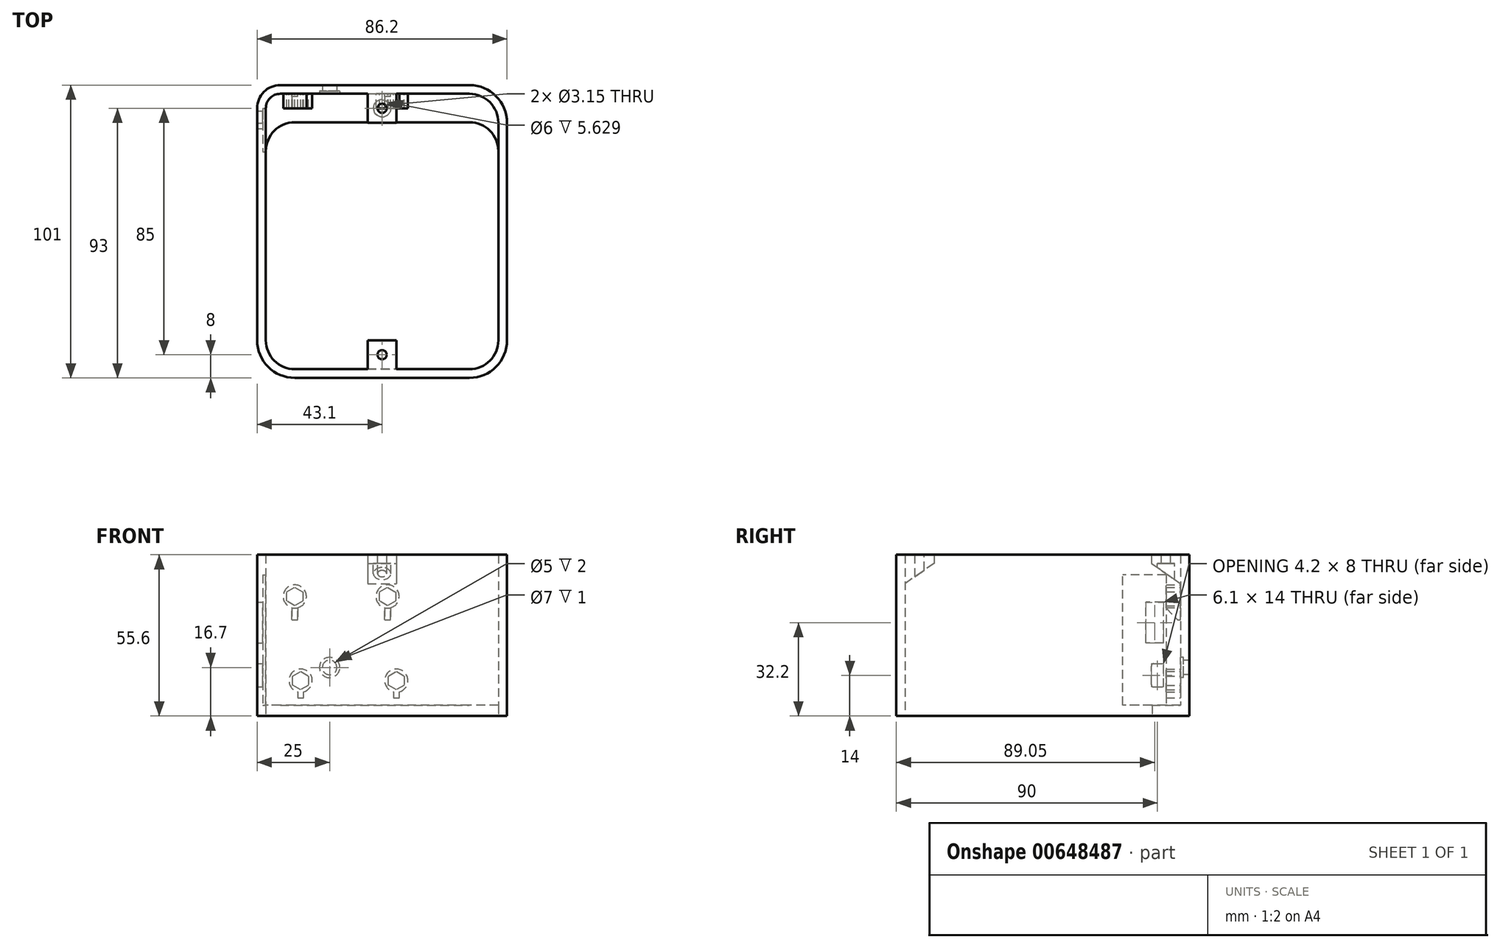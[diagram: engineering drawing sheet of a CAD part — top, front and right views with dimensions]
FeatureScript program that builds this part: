
annotation { "Feature Type Name" : "Feature", "Feature Type Description" : "" }
export const myFeature = defineFeature(function(context is Context, id is Id, definition is map)
    precondition{}
    {
        {
            var Q0;
            Q0=qCreatedBy(makeId("Top.planeOp"),FACE);
            var sketch = newSketch(context, id + "F0", { "sketchPlane" : qUnion([Q0])});
            skLineSegment(sketch, "E0.bottom", {"start": v(30.1, 37.7) * mm, "end": v(-30.1, 37.7) * mm});
            skLineSegment(sketch, "E0.top", {"start": v(30.1, -47.5) * mm, "end": v(-30.1, -47.5) * mm});
            skLineSegment(sketch, "E0.left", {"start": v(40.1, 27.7) * mm, "end": v(40.1, -37.5) * mm});
            skLineSegment(sketch, "E0.right", {"start": v(-40.1, 27.7) * mm, "end": v(-40.1, -37.5) * mm});
            skPoint(sketch, "E0.middle", {"position": v(0, 0) * mm});
            skPoint(sketch, "E1.visualSharp", {"position": v(-40.1, 37.7) * mm});
            skArc(sketch, "E1.filletArc", {"start": v(-30.1, 37.7) * mm, "mid": v(-37.17, 34.77) * mm, "end": v(-40.1, 27.7) * mm});
            skPoint(sketch, "E2.visualSharp", {"position": v(-40.1, -47.5) * mm});
            skArc(sketch, "E2.filletArc", {"start": v(-40.1, -37.5) * mm, "mid": v(-37.17, -44.57) * mm, "end": v(-30.1, -47.5) * mm});
            skPoint(sketch, "E3.visualSharp", {"position": v(40.1, -47.5) * mm});
            skArc(sketch, "E3.filletArc", {"start": v(30.1, -47.5) * mm, "mid": v(37.17, -44.57) * mm, "end": v(40.1, -37.5) * mm});
            skPoint(sketch, "E4.visualSharp", {"position": v(40.1, 37.7) * mm});
            skArc(sketch, "E4.filletArc", {"start": v(40.1, 27.7) * mm, "mid": v(37.17, 34.77) * mm, "end": v(30.1, 37.7) * mm});
            skLineSegment(sketch, "E5.bottom", {"start": v(30.1, 50.5) * mm, "end": v(-35.1, 50.5) * mm});
            skLineSegment(sketch, "E5.top", {"start": v(30.1, -50.5) * mm, "end": v(-30.1, -50.5) * mm});
            skLineSegment(sketch, "E5.left", {"start": v(43.1, 37.5) * mm, "end": v(43.1, -37.5) * mm});
            skLineSegment(sketch, "E5.right", {"start": v(-43.1, 42.5) * mm, "end": v(-43.1, -37.5) * mm});
            skPoint(sketch, "E6.visualSharp", {"position": v(-43.1, 50.5) * mm});
            skArc(sketch, "E6.filletArc", {"start": v(-35.1, 50.5) * mm, "mid": v(-40.76, 48.16) * mm, "end": v(-43.1, 42.5) * mm});
            skPoint(sketch, "E7.visualSharp", {"position": v(43.1, 50.5) * mm});
            skArc(sketch, "E7.filletArc", {"start": v(43.1, 37.5) * mm, "mid": v(39.3, 46.7) * mm, "end": v(30.1, 50.5) * mm});
            skPoint(sketch, "E8.visualSharp", {"position": v(43.1, -50.5) * mm});
            skArc(sketch, "E8.filletArc", {"start": v(30.1, -50.5) * mm, "mid": v(39.3, -46.7) * mm, "end": v(43.1, -37.5) * mm});
            skPoint(sketch, "E9.visualSharp", {"position": v(-43.1, -50.5) * mm});
            skArc(sketch, "E9.filletArc", {"start": v(-43.1, -37.5) * mm, "mid": v(-39.3, -46.7) * mm, "end": v(-30.1, -50.5) * mm});
            skLineSegment(sketch, "E10", {"start": v(30.1, 47.5) * mm, "end": v(-35.1, 47.5) * mm});
            skArc(sketch, "E11", {"start": v(30.1, 47.5) * mm, "mid": v(37.17, 44.57) * mm, "end": v(40.1, 37.5) * mm});
            skLineSegment(sketch, "E12", {"start": v(40.1, 27.7) * mm, "end": v(40.1, 37.5) * mm});
            skArc(sketch, "E13", {"start": v(-35.1, 47.5) * mm, "mid": v(-38.64, 46.04) * mm, "end": v(-40.1, 42.5) * mm});
            skLineSegment(sketch, "E14", {"start": v(-40.1, 42.5) * mm, "end": v(-40.1, 27.7) * mm});
            skSolve(sketch);
        }
        {
            var Q0;
            Q0=makeQuery(id+"F0.imprint","IMPRINT",FACE,{"disambiguationData":[TD([[makeQuery(id+"F0.imprint","IMPRINT",EDGE,{"derivedFrom":sQuery(id+"F0.wireOp",EDGE,"E0.bottom")}),-1.0]])]});
            var Q1;
            Q1=makeQuery(id+"F0.imprint","IMPRINT",FACE,{"disambiguationData":[TD([[makeQuery(id+"F0.imprint","IMPRINT",EDGE,{"derivedFrom":sQuery(id+"F0.wireOp",EDGE,"E0.top")}),1.0]])]});
            extrude(context, id + "F1", {"entities" : qUnion([Q0, Q1]), "depth" : 3.7 * mm, "offsetDistance" : 25 * mm});
        }
        {
            var Q0;
            Q0=makeQuery(id+"F0.imprint","IMPRINT",FACE,{"disambiguationData":[TD([[makeQuery(id+"F0.imprint","IMPRINT",EDGE,{"derivedFrom":sQuery(id+"F0.wireOp",EDGE,"E0.top")}),1.0]])]});
            extrude(context, id + "F2", {"entities" : qUnion([Q0]), "operationType" : NewBodyOperationType.ADD, "depth" : (3.5 + 52.1) * mm, "offsetDistance" : 25 * mm});
        }
        {
            var Q0;
            {var subQ0=sQuery(id+"F0.wireOp",EDGE,"E0.left");Q0=makeQuery(id+"F2.boolean.opBoolean","MERGE",FACE,{"derivedFrom":[makeQuery(id+"F1.opExtrude","SWEPT_FACE",FACE,{"disambiguationData":[OSD([subQ0])]}),makeQuery(id+"F2.opExtrude","SWEPT_FACE",FACE,{"disambiguationData":[OSD([subQ0,sQuery(id+"F0.wireOp",EDGE,"E12")])]})]});}
            cPlane(context, id + "F3", {"entities" : qUnion([Q0]), "cplaneType" : CPlaneType.OFFSET, "offset" : 40.1 * mm, "width" : 150 * mm, "height" : 150 * mm});
        }
        {
            var Q0;
            Q0=qCreatedBy(id+"F3.planeOp",FACE);
            var sketch = newSketch(context, id + "F4", { "sketchPlane" : qUnion([Q0])});
            skLineSegment(sketch, "E15", {"start": v(47.5, 55.6) * mm, "end": v(47.5, 45.6) * mm});
            skLineSegment(sketch, "E16", {"start": v(47.5, 55.6) * mm, "end": v(37.5, 55.6) * mm});
            skLineSegment(sketch, "E17", {"start": v(37.5, 55.6) * mm, "end": v(37.5, 52.6) * mm});
            skLineSegment(sketch, "E18.MirrorCS", {"start": v(-37.5, 55.6) * mm, "end": v(-37.5, 52.6) * mm});
            skLineSegment(sketch, "E19.MirrorCS", {"start": v(-47.5, 55.6) * mm, "end": v(-37.5, 55.6) * mm});
            skLineSegment(sketch, "E20.MirrorCS", {"start": v(-47.5, 55.6) * mm, "end": v(-47.5, 45.6) * mm});
            skLineSegment(sketch, "E21", {"start": v(37.5, 52.6) * mm, "end": v(47.5, 45.6) * mm});
            skLineSegment(sketch, "E22.MirrorCS", {"start": v(-37.5, 52.6) * mm, "end": v(-47.5, 45.6) * mm});
            skSolve(sketch);
        }
        {
            var Q0;
            Q0=makeQuery(id+"F4.imprint","IMPRINT",FACE,{"disambiguationData":[TD([[makeQuery(id+"F4.imprint","IMPRINT",EDGE,{"derivedFrom":sQuery(id+"F4.wireOp",EDGE,"E15")}),-1.0]])]});
            var Q1;
            Q1=makeQuery(id+"F4.imprint","IMPRINT",FACE,{"disambiguationData":[TD([[makeQuery(id+"F4.imprint","IMPRINT",EDGE,{"derivedFrom":sQuery(id+"F4.wireOp",EDGE,"E18.MirrorCS")}),-1.0]])]});
            extrude(context, id + "F5", {"entities" : qUnion([Q0, Q1]), "operationType" : NewBodyOperationType.ADD, "endBound" : BoundingType.SYMMETRIC, "depth" : 10 * mm, "offsetDistance" : 25 * mm});
        }
        {
            var Q0;
            Q0=makeQuery(id+"F5.boolean.opBoolean","MERGE",FACE,{"derivedFrom":[makeQuery(id+"F2.opExtrude","CAP_FACE",FACE,{"disambiguationData":[OSD([sQuery(id+"F0.wireOp",EDGE,"E0.top"),sQuery(id+"F0.wireOp",EDGE,"E0.left"),sQuery(id+"F0.wireOp",EDGE,"E0.right"),sQuery(id+"F0.wireOp",EDGE,"E2.filletArc"),sQuery(id+"F0.wireOp",EDGE,"E3.filletArc"),sQuery(id+"F0.wireOp",EDGE,"E5.bottom"),sQuery(id+"F0.wireOp",EDGE,"E5.top"),sQuery(id+"F0.wireOp",EDGE,"E5.left"),sQuery(id+"F0.wireOp",EDGE,"E5.right"),sQuery(id+"F0.wireOp",EDGE,"E6.filletArc"),sQuery(id+"F0.wireOp",EDGE,"E7.filletArc"),sQuery(id+"F0.wireOp",EDGE,"E8.filletArc"),sQuery(id+"F0.wireOp",EDGE,"E9.filletArc"),sQuery(id+"F0.wireOp",EDGE,"E10"),sQuery(id+"F0.wireOp",EDGE,"E11"),sQuery(id+"F0.wireOp",EDGE,"b7809514-09bd-4c88-a942-83dfe2632a91"),sQuery(id+"F0.wireOp",EDGE,"Me8D9nFj-TIqi-SRSQ-5CqU-nn7HwhDE9VmM"),sQuery(id+"F0.wireOp",EDGE,"E12")])],"isStart":false}),makeQuery(id+"F5.opExtrude","SWEPT_FACE",FACE,{"disambiguationData":[OSD([sQuery(id+"F4.wireOp",EDGE,"E16")])]}),makeQuery(id+"F5.opExtrude","SWEPT_FACE",FACE,{"disambiguationData":[OSD([sQuery(id+"F4.wireOp",EDGE,"E19.MirrorCS")])]})]});
            var sketch = newSketch(context, id + "F6", { "sketchPlane" : qUnion([Q0])});
            skPoint(sketch, "E23", {"position": v(0, 42.5) * mm});
            skPoint(sketch, "E24.MirrorP", {"position": v(0, -42.5) * mm});
            skSolve(sketch);
        }
        {
            var Q0;
            Q0=sQuery(id+"F6.wireOp",VERTEX,"E23");
            var Q1;
            Q1=sQuery(id+"F6.wireOp",VERTEX,"E24.MirrorP");
            var Q2;
            Q2=makeQuery(id+"F1.opExtrude","SWEPT_BODY",BODY,{"disambiguationData":[OSD([sQuery(id+"F0.wireOp",EDGE,"E0.bottom"),sQuery(id+"F0.wireOp",EDGE,"E0.top"),sQuery(id+"F0.wireOp",EDGE,"E0.left"),sQuery(id+"F0.wireOp",EDGE,"E0.right"),sQuery(id+"F0.wireOp",EDGE,"E1.filletArc"),sQuery(id+"F0.wireOp",EDGE,"E2.filletArc"),sQuery(id+"F0.wireOp",EDGE,"E3.filletArc"),sQuery(id+"F0.wireOp",EDGE,"E4.filletArc"),sQuery(id+"F0.wireOp",EDGE,"E5.bottom"),sQuery(id+"F0.wireOp",EDGE,"E5.top"),sQuery(id+"F0.wireOp",EDGE,"E5.left"),sQuery(id+"F0.wireOp",EDGE,"E5.right"),sQuery(id+"F0.wireOp",EDGE,"E6.filletArc"),sQuery(id+"F0.wireOp",EDGE,"E7.filletArc"),sQuery(id+"F0.wireOp",EDGE,"E8.filletArc"),sQuery(id+"F0.wireOp",EDGE,"E9.filletArc")])]});
            hole(context, id + "F7", {"style" : HoleStyle.SIMPLE, "endStyle" : HoleEndStyle.BLIND, "standardTappedOrClearance" : lookupTablePath({ "standard" : "ISO", "fit" : "Close", "size" : "M3", "type" : "Clearance" }), "standardBlindInLast" : lookupTablePath({ "fit" : "Close", "standard" : "ISO", "size" : "M3", "type" : "Clearance" }), "holeDiameter" : 3.15 * mm, "majorDiameter" : 5 * mm, "holeDepth" : 10 * mm, "isTappedThrough" : true, "tappedDepth" : 17.6 * mm, "tapClearance" : 3, "locations" : qUnion([Q0, Q1]), "scope" : qUnion([Q2])});
        }
        {
            var Q0;
            Q0=makeQuery(id+"F5.boolean.opBoolean","MERGE",FACE,{"derivedFrom":[makeQuery(id+"F2.opExtrude","CAP_FACE",FACE,{"disambiguationData":[OSD([sQuery(id+"F0.wireOp",EDGE,"E0.top"),sQuery(id+"F0.wireOp",EDGE,"E0.left"),sQuery(id+"F0.wireOp",EDGE,"E0.right"),sQuery(id+"F0.wireOp",EDGE,"E2.filletArc"),sQuery(id+"F0.wireOp",EDGE,"E3.filletArc"),sQuery(id+"F0.wireOp",EDGE,"E5.bottom"),sQuery(id+"F0.wireOp",EDGE,"E5.top"),sQuery(id+"F0.wireOp",EDGE,"E5.left"),sQuery(id+"F0.wireOp",EDGE,"E5.right"),sQuery(id+"F0.wireOp",EDGE,"E6.filletArc"),sQuery(id+"F0.wireOp",EDGE,"E7.filletArc"),sQuery(id+"F0.wireOp",EDGE,"E8.filletArc"),sQuery(id+"F0.wireOp",EDGE,"E9.filletArc"),sQuery(id+"F0.wireOp",EDGE,"E10"),sQuery(id+"F0.wireOp",EDGE,"E11"),sQuery(id+"F0.wireOp",EDGE,"b7809514-09bd-4c88-a942-83dfe2632a91"),sQuery(id+"F0.wireOp",EDGE,"Me8D9nFj-TIqi-SRSQ-5CqU-nn7HwhDE9VmM"),sQuery(id+"F0.wireOp",EDGE,"E12")])],"isStart":false}),makeQuery(id+"F5.opExtrude","SWEPT_FACE",FACE,{"disambiguationData":[OSD([sQuery(id+"F4.wireOp",EDGE,"E16")])]}),makeQuery(id+"F5.opExtrude","SWEPT_FACE",FACE,{"disambiguationData":[OSD([sQuery(id+"F4.wireOp",EDGE,"E19.MirrorCS")])]})]});
            cPlane(context, id + "F8", {"entities" : qUnion([Q0]), "cplaneType" : CPlaneType.OFFSET, "offset" : 3 * mm, "oppositeDirection" : true, "width" : 150 * mm, "height" : 150 * mm});
        }
        {
            var Q0;
            Q0=qCreatedBy(id+"F8.planeOp",FACE);
            var sketch = newSketch(context, id + "F9", { "sketchPlane" : qUnion([Q0])});
            skCircle(sketch, "E25", {"center": v(0, 42.5) * mm, "radius": 3 * mm});
            skCircle(sketch, "E26.MirrorC", {"center": v(0, -42.5) * mm, "radius": 3 * mm});
            skSolve(sketch);
        }
        {
            var Q0;
            Q0=makeQuery(id+"F9.imprint","IMPRINT",FACE,{"disambiguationData":[TD([[makeQuery(id+"F9.imprint","IMPRINT",EDGE,{"derivedFrom":sQuery(id+"F9.wireOp",EDGE,"E25")}),1.0]])]});
            var Q1;
            Q1=makeQuery(id+"F9.imprint","IMPRINT",FACE,{"disambiguationData":[TD([[makeQuery(id+"F9.imprint","IMPRINT",EDGE,{"derivedFrom":sQuery(id+"F9.wireOp",EDGE,"E26.MirrorC")}),-1.0]])]});
            extrude(context, id + "F10", {"entities" : qUnion([Q0, Q1]), "operationType" : NewBodyOperationType.REMOVE, "oppositeDirection" : true, "depth" : 10 * mm, "offsetDistance" : 25 * mm});
        }
        {
            var Q0;
            Q0=makeQuery(id+"F2.opExtrude","SWEPT_FACE",FACE,{"disambiguationData":[OSD([sQuery(id+"F0.wireOp",EDGE,"E10")])]});
            var sketch = newSketch(context, id + "F11", { "sketchPlane" : qUnion([Q0])});
            skLineSegment(sketch, "E27.bottom", {"start": v(-30.1, 12.2) * mm, "end": v(4.9, 12.2) * mm, "construction": true});
            skLineSegment(sketch, "E27.top", {"start": v(-30.1, 41.2) * mm, "end": v(4.9, 41.2) * mm, "construction": true});
            skLineSegment(sketch, "E27.left", {"start": v(-30.1, 12.2) * mm, "end": v(-30.1, 41.2) * mm, "construction": true});
            skLineSegment(sketch, "E27.right", {"start": v(4.9, 12.2) * mm, "end": v(4.9, 41.2) * mm, "construction": true});
            skPoint(sketch, "E28", {"position": v(-28.1, 12.2) * mm});
            skPoint(sketch, "E29", {"position": v(1.9, 41.2) * mm});
            skCircle(sketch, "E30", {"center": v(-30.1, 41.2) * mm, "radius": 4 * mm});
            skCircle(sketch, "E31", {"center": v(1.9, 41.2) * mm, "radius": 4 * mm});
            skCircle(sketch, "E32", {"center": v(-28.1, 12.2) * mm, "radius": 4 * mm});
            skCircle(sketch, "E33", {"center": v(4.9, 12.2) * mm, "radius": 4 * mm});
            skCircle(sketch, "E34.cCircle", {"center": v(1.9, 41.2) * mm, "radius": 2.75 * mm, "construction": true});
            skLineSegment(sketch, "E34.0", {"start": v(4.65, 42.79) * mm, "end": v(4.65, 39.61) * mm});
            skLineSegment(sketch, "E34.1", {"start": v(4.65, 39.61) * mm, "end": v(1.9, 38.02) * mm});
            skLineSegment(sketch, "E34.2", {"start": v(1.9, 38.02) * mm, "end": v(-0.85, 39.61) * mm});
            skLineSegment(sketch, "E34.3", {"start": v(-0.85, 39.61) * mm, "end": v(-0.85, 42.79) * mm});
            skLineSegment(sketch, "E34.4", {"start": v(-0.85, 42.79) * mm, "end": v(1.9, 44.38) * mm});
            skLineSegment(sketch, "E34.5", {"start": v(1.9, 44.38) * mm, "end": v(4.65, 42.79) * mm});
            skPoint(sketch, "E34.0.midPoint", {"position": v(4.65, 41.2) * mm});
            skCircle(sketch, "E35.cCircle", {"center": v(-30.1, 41.2) * mm, "radius": 2.75 * mm, "construction": true});
            skLineSegment(sketch, "E35.0", {"start": v(-27.35, 42.79) * mm, "end": v(-27.35, 39.61) * mm});
            skLineSegment(sketch, "E35.1", {"start": v(-27.35, 39.61) * mm, "end": v(-30.1, 38.02) * mm});
            skLineSegment(sketch, "E35.2", {"start": v(-30.1, 38.02) * mm, "end": v(-32.85, 39.61) * mm});
            skLineSegment(sketch, "E35.3", {"start": v(-32.85, 39.61) * mm, "end": v(-32.85, 42.79) * mm});
            skLineSegment(sketch, "E35.4", {"start": v(-32.85, 42.79) * mm, "end": v(-30.1, 44.38) * mm});
            skLineSegment(sketch, "E35.5", {"start": v(-30.1, 44.38) * mm, "end": v(-27.35, 42.79) * mm});
            skPoint(sketch, "E35.0.midPoint", {"position": v(-27.35, 41.2) * mm});
            skCircle(sketch, "E36.cCircle", {"center": v(-28.1, 12.2) * mm, "radius": 2.75 * mm, "construction": true});
            skLineSegment(sketch, "E36.0", {"start": v(-25.35, 13.79) * mm, "end": v(-25.35, 10.61) * mm});
            skLineSegment(sketch, "E36.1", {"start": v(-25.35, 10.61) * mm, "end": v(-28.1, 9.02) * mm});
            skLineSegment(sketch, "E36.2", {"start": v(-28.1, 9.02) * mm, "end": v(-30.85, 10.61) * mm});
            skLineSegment(sketch, "E36.3", {"start": v(-30.85, 10.61) * mm, "end": v(-30.85, 13.79) * mm});
            skLineSegment(sketch, "E36.4", {"start": v(-30.85, 13.79) * mm, "end": v(-28.1, 15.38) * mm});
            skLineSegment(sketch, "E36.5", {"start": v(-28.1, 15.38) * mm, "end": v(-25.35, 13.79) * mm});
            skPoint(sketch, "E36.0.midPoint", {"position": v(-25.35, 12.2) * mm});
            skCircle(sketch, "E37.cCircle", {"center": v(4.9, 12.2) * mm, "radius": 2.75 * mm, "construction": true});
            skLineSegment(sketch, "E37.0", {"start": v(7.65, 13.79) * mm, "end": v(7.65, 10.61) * mm});
            skLineSegment(sketch, "E37.1", {"start": v(7.65, 10.61) * mm, "end": v(4.9, 9.02) * mm});
            skLineSegment(sketch, "E37.2", {"start": v(4.9, 9.02) * mm, "end": v(2.15, 10.61) * mm});
            skLineSegment(sketch, "E37.3", {"start": v(2.15, 10.61) * mm, "end": v(2.15, 13.79) * mm});
            skLineSegment(sketch, "E37.4", {"start": v(2.15, 13.79) * mm, "end": v(4.9, 15.38) * mm});
            skLineSegment(sketch, "E37.5", {"start": v(4.9, 15.38) * mm, "end": v(7.65, 13.79) * mm});
            skPoint(sketch, "E37.0.midPoint", {"position": v(7.65, 12.2) * mm});
            skCircle(sketch, "E38", {"center": v(-18.1, 16.7) * mm, "radius": 2.5 * mm});
            skCircle(sketch, "E39", {"center": v(-18.1, 16.7) * mm, "radius": 3.5 * mm});
            skLineSegment(sketch, "E40", {"start": v(-31.1, 37.33) * mm, "end": v(-31.1, 33.2) * mm});
            skLineSegment(sketch, "E41", {"start": v(-31.1, 33.2) * mm, "end": v(-29.1, 33.2) * mm});
            skLineSegment(sketch, "E42", {"start": v(-29.1, 33.2) * mm, "end": v(-29.1, 37.33) * mm});
            skLineSegment(sketch, "E43", {"start": v(0.9, 37.33) * mm, "end": v(0.9, 33.2) * mm});
            skLineSegment(sketch, "E44", {"start": v(0.9, 33.2) * mm, "end": v(2.9, 33.2) * mm});
            skLineSegment(sketch, "E45", {"start": v(2.9, 33.2) * mm, "end": v(2.9, 37.33) * mm});
            skLineSegment(sketch, "E46", {"start": v(-29.1, 8.33) * mm, "end": v(-29.1, 6.2) * mm});
            skLineSegment(sketch, "E47", {"start": v(-29.1, 6.2) * mm, "end": v(-27.1, 6.2) * mm});
            skLineSegment(sketch, "E48", {"start": v(-27.1, 6.2) * mm, "end": v(-27.1, 8.33) * mm});
            skLineSegment(sketch, "E49", {"start": v(3.9, 8.33) * mm, "end": v(3.9, 6.2) * mm});
            skLineSegment(sketch, "E50", {"start": v(3.9, 6.2) * mm, "end": v(5.9, 6.2) * mm});
            skLineSegment(sketch, "E51", {"start": v(5.9, 6.2) * mm, "end": v(5.9, 8.33) * mm});
            skSolve(sketch);
        }
        {
            var Q0;
            {var subQ0=sQuery(id+"F11.wireOp",EDGE,"E30");var subQ1=makeQuery(id+"F2.opExtrude","SWEPT_EDGE",EDGE,{"disambiguationData":[OSD([sQuery(id+"F0.wireOp",EDGE,"E10"),sQuery(id+"F0.wireOp",EDGE,"b7809514-09bd-4c88-a942-83dfe2632a91")])]});var subQ2=makeQuery(id+"F11.imprint","INTERSECT",VERTEX,{"disambiguationData":[OD(0.0)],"derivedFrom":[subQ1,subQ0]});Q0=makeQuery(id+"F11.imprint","IMPRINT",FACE,{"disambiguationData":[TD([[makeQuery(id+"F11.imprint","IMPRINT",EDGE,{"disambiguationData":[TD([[subQ2,-1.0]])],"derivedFrom":subQ0}),1.0]])]});}
            var Q1;
            {var subQ0=sQuery(id+"F11.wireOp",EDGE,"E30");var subQ1=makeQuery(id+"F2.opExtrude","SWEPT_EDGE",EDGE,{"disambiguationData":[OSD([sQuery(id+"F0.wireOp",EDGE,"E10"),sQuery(id+"F0.wireOp",EDGE,"b7809514-09bd-4c88-a942-83dfe2632a91")])]});var subQ2=makeQuery(id+"F11.imprint","INTERSECT",VERTEX,{"disambiguationData":[OD(0.0)],"derivedFrom":[subQ1,subQ0]});Q1=makeQuery(id+"F11.imprint","IMPRINT",FACE,{"disambiguationData":[TD([[makeQuery(id+"F11.imprint","IMPRINT",EDGE,{"disambiguationData":[TD([[subQ2,1.0]])],"derivedFrom":subQ0}),1.0]])]});}
            var Q2;
            Q2=makeQuery(id+"F11.imprint","IMPRINT",FACE,{"disambiguationData":[TD([[makeQuery(id+"F11.imprint","IMPRINT",EDGE,{"derivedFrom":sQuery(id+"F11.wireOp",EDGE,"E31")}),1.0]])]});
            var Q3;
            Q3=makeQuery(id+"F11.imprint","IMPRINT",FACE,{"disambiguationData":[TD([[makeQuery(id+"F11.imprint","IMPRINT",EDGE,{"derivedFrom":sQuery(id+"F11.wireOp",EDGE,"E33")}),1.0]])]});
            var Q4;
            {var subQ0=sQuery(id+"F11.wireOp",EDGE,"E32");var subQ1=makeQuery(id+"F2.opExtrude","SWEPT_EDGE",EDGE,{"disambiguationData":[OSD([sQuery(id+"F0.wireOp",EDGE,"E10"),sQuery(id+"F0.wireOp",EDGE,"b7809514-09bd-4c88-a942-83dfe2632a91")])]});var subQ2=makeQuery(id+"F11.imprint","INTERSECT",VERTEX,{"disambiguationData":[OD(0.0)],"derivedFrom":[subQ1,subQ0]});Q4=makeQuery(id+"F11.imprint","IMPRINT",FACE,{"disambiguationData":[TD([[makeQuery(id+"F11.imprint","IMPRINT",EDGE,{"disambiguationData":[TD([[subQ2,1.0]])],"derivedFrom":subQ0}),1.0]])]});}
            var Q5;
            {var subQ0=sQuery(id+"F11.wireOp",EDGE,"E32");var subQ1=makeQuery(id+"F2.opExtrude","SWEPT_EDGE",EDGE,{"disambiguationData":[OSD([sQuery(id+"F0.wireOp",EDGE,"E10"),sQuery(id+"F0.wireOp",EDGE,"b7809514-09bd-4c88-a942-83dfe2632a91")])]});var subQ2=makeQuery(id+"F11.imprint","INTERSECT",VERTEX,{"disambiguationData":[OD(0.0)],"derivedFrom":[subQ1,subQ0]});Q5=makeQuery(id+"F11.imprint","IMPRINT",FACE,{"disambiguationData":[TD([[makeQuery(id+"F11.imprint","IMPRINT",EDGE,{"disambiguationData":[TD([[subQ2,-1.0]])],"derivedFrom":subQ0}),1.0]])]});}
            var Q6;
            {var subQ0=sQuery(id+"F11.wireOp",EDGE,"E40");Q6=makeQuery(id+"F11.imprint","IMPRINT",FACE,{"disambiguationData":[TD([[makeQuery(id+"F11.imprint","IMPRINT",EDGE,{"derivedFrom":subQ0}),1.0]])]});}
            var Q7;
            {var subQ0=sQuery(id+"F11.wireOp",EDGE,"E42");Q7=makeQuery(id+"F11.imprint","IMPRINT",FACE,{"disambiguationData":[TD([[makeQuery(id+"F11.imprint","IMPRINT",EDGE,{"derivedFrom":subQ0}),1.0]])]});}
            var Q8;
            {var subQ0=sQuery(id+"F11.wireOp",EDGE,"E43");Q8=makeQuery(id+"F11.imprint","IMPRINT",FACE,{"disambiguationData":[TD([[makeQuery(id+"F11.imprint","IMPRINT",EDGE,{"derivedFrom":subQ0}),1.0]])]});}
            var Q9;
            {var subQ0=sQuery(id+"F11.wireOp",EDGE,"E50");Q9=makeQuery(id+"F11.imprint","IMPRINT",FACE,{"disambiguationData":[TD([[makeQuery(id+"F11.imprint","IMPRINT",EDGE,{"derivedFrom":subQ0}),1.0]])]});}
            var Q10;
            {var subQ0=sQuery(id+"F11.wireOp",EDGE,"E49");var subQ1=sQuery(id+"F11.wireOp",EDGE,"E33");var subQ2=makeQuery(id+"F11.imprint","INTERSECT",VERTEX,{"derivedFrom":[subQ1,subQ0]});Q10=makeQuery(id+"F11.imprint","IMPRINT",FACE,{"disambiguationData":[TD([[makeQuery(id+"F11.imprint","IMPRINT",EDGE,{"disambiguationData":[TD([[subQ2,-1.0]])],"derivedFrom":subQ1}),-1.0]])]});}
            var Q11;
            {var subQ0=sQuery(id+"F11.wireOp",EDGE,"E47");Q11=makeQuery(id+"F11.imprint","IMPRINT",FACE,{"disambiguationData":[TD([[makeQuery(id+"F11.imprint","IMPRINT",EDGE,{"derivedFrom":subQ0}),1.0]])]});}
            var Q12;
            {var subQ0=sQuery(id+"F11.wireOp",EDGE,"E46");var subQ1=sQuery(id+"F11.wireOp",EDGE,"E32");var subQ2=makeQuery(id+"F11.imprint","INTERSECT",VERTEX,{"derivedFrom":[subQ1,subQ0]});Q12=makeQuery(id+"F11.imprint","IMPRINT",FACE,{"disambiguationData":[TD([[makeQuery(id+"F11.imprint","IMPRINT",EDGE,{"disambiguationData":[TD([[subQ2,-1.0]])],"derivedFrom":subQ1}),-1.0]])]});}
            extrude(context, id + "F12", {"entities" : qUnion([Q0, Q1, Q2, Q3, Q4, Q5, Q6, Q7, Q8, Q9, Q10, Q11, Q12]), "operationType" : NewBodyOperationType.ADD, "depth" : 5 * mm, "offsetDistance" : 25 * mm});
        }
        {
            var Q0;
            Q0=makeQuery(id+"F11.imprint","IMPRINT",FACE,{"disambiguationData":[TD([[makeQuery(id+"F11.imprint","IMPRINT",EDGE,{"derivedFrom":sQuery(id+"F11.wireOp",EDGE,"E38")}),1.0]])]});
            extrude(context, id + "F13", {"entities" : qUnion([Q0]), "operationType" : NewBodyOperationType.REMOVE, "oppositeDirection" : true, "depth" : 25 * mm, "offsetDistance" : 25 * mm});
        }
        {
            var Q0;
            Q0=makeQuery(id+"F11.imprint","IMPRINT",FACE,{"disambiguationData":[TD([[makeQuery(id+"F11.imprint","IMPRINT",EDGE,{"derivedFrom":sQuery(id+"F11.wireOp",EDGE,"E38")}),-1.0]])]});
            var Q1;
            Q1=makeQuery(id+"F11.imprint","IMPRINT",FACE,{"disambiguationData":[TD([[makeQuery(id+"F11.imprint","IMPRINT",EDGE,{"derivedFrom":sQuery(id+"F11.wireOp",EDGE,"E38")}),1.0]])]});
            extrude(context, id + "F14", {"entities" : qUnion([Q0, Q1]), "operationType" : NewBodyOperationType.REMOVE, "oppositeDirection" : true, "depth" : 1 * mm, "offsetDistance" : 25 * mm});
        }
        {
            var Q0;
            Q0=makeQuery(id+"F12.opExtrude","CAP_EDGE",EDGE,{"disambiguationData":[OSD([sQuery(id+"F11.wireOp",EDGE,"E44")])],"isStart":false});
            var Q1;
            Q1=makeQuery(id+"F12.opExtrude","CAP_EDGE",EDGE,{"disambiguationData":[OSD([sQuery(id+"F11.wireOp",EDGE,"E41")])],"isStart":false});
            chamfer(context, id + "F15", {"entities" : qUnion([Q0, Q1]), "width" : 4 * mm, "tangentPropagation" : true});
        }
        {
            var Q0;
            {var subQ0=sQuery(id+"F0.wireOp",EDGE,"E0.right");Q0=makeQuery(id+"F2.boolean.opBoolean","MERGE",FACE,{"derivedFrom":[makeQuery(id+"F1.opExtrude","SWEPT_FACE",FACE,{"disambiguationData":[OSD([subQ0])]}),makeQuery(id+"F2.opExtrude","SWEPT_FACE",FACE,{"disambiguationData":[OSD([subQ0,sQuery(id+"F0.wireOp",EDGE,"E14")])]})]});}
            var sketch = newSketch(context, id + "F16", { "sketchPlane" : qUnion([Q0])});
            skLineSegment(sketch, "E52", {"start": v(42.5, 55.6) * mm, "end": v(42.5, 3.7) * mm, "construction": true});
            skLineSegment(sketch, "E53.bottom", {"start": v(42.5, 3.7) * mm, "end": v(27.5, 3.7) * mm});
            skLineSegment(sketch, "E53.top", {"start": v(42.5, 48.7) * mm, "end": v(27.5, 48.7) * mm});
            skLineSegment(sketch, "E53.left", {"start": v(42.5, 3.7) * mm, "end": v(42.5, 48.7) * mm});
            skLineSegment(sketch, "E53.right", {"start": v(27.5, 3.7) * mm, "end": v(27.5, 48.7) * mm});
            skLineSegment(sketch, "E54.bottom", {"start": v(37.4, 10) * mm, "end": v(41.6, 10) * mm});
            skLineSegment(sketch, "E54.top", {"start": v(37.4, 18) * mm, "end": v(41.6, 18) * mm});
            skLineSegment(sketch, "E54.left", {"start": v(37.4, 10) * mm, "end": v(37.4, 18) * mm});
            skLineSegment(sketch, "E54.right", {"start": v(41.6, 10) * mm, "end": v(41.6, 18) * mm});
            skLineSegment(sketch, "E55.bottom", {"start": v(41.6, 25.2) * mm, "end": v(35.5, 25.2) * mm});
            skLineSegment(sketch, "E55.top", {"start": v(41.6, 39.2) * mm, "end": v(35.5, 39.2) * mm});
            skLineSegment(sketch, "E55.left", {"start": v(41.6, 25.2) * mm, "end": v(41.6, 39.2) * mm});
            skLineSegment(sketch, "E55.right", {"start": v(35.5, 25.2) * mm, "end": v(35.5, 39.2) * mm});
            skSolve(sketch);
        }
        {
            var Q0;
            Q0=makeQuery(id+"F16.imprint","IMPRINT",FACE,{"disambiguationData":[TD([[makeQuery(id+"F16.imprint","IMPRINT",EDGE,{"derivedFrom":sQuery(id+"F16.wireOp",EDGE,"E53.top")}),1.0]])]});
            extrude(context, id + "F17", {"entities" : qUnion([Q0]), "operationType" : NewBodyOperationType.REMOVE, "oppositeDirection" : true, "depth" : 1 * mm, "offsetDistance" : 25 * mm});
        }
        {
            var Q0;
            Q0=makeQuery(id+"F16.imprint","IMPRINT",FACE,{"disambiguationData":[TD([[makeQuery(id+"F16.imprint","IMPRINT",EDGE,{"derivedFrom":sQuery(id+"F16.wireOp",EDGE,"E55.bottom")}),-1.0]])]});
            var Q1;
            Q1=makeQuery(id+"F16.imprint","IMPRINT",FACE,{"disambiguationData":[TD([[makeQuery(id+"F16.imprint","IMPRINT",EDGE,{"derivedFrom":sQuery(id+"F16.wireOp",EDGE,"E54.bottom")}),1.0]])]});
            extrude(context, id + "F18", {"entities" : qUnion([Q0, Q1]), "operationType" : NewBodyOperationType.REMOVE, "oppositeDirection" : true, "depth" : 3 * mm, "offsetDistance" : 25 * mm});
        }
        {
            var Q0;
            Q0=makeQuery(id+"F18.boolean.opBoolean","COPY",EDGE,{"derivedFrom":makeQuery(id+"F18.opExtrude","SWEPT_EDGE",EDGE,{"disambiguationData":[OSD([sQuery(id+"F16.wireOp",EDGE,"E54.top"),sQuery(id+"F16.wireOp",EDGE,"E54.left")])]})});
            var Q1;
            Q1=makeQuery(id+"F18.boolean.opBoolean","COPY",EDGE,{"derivedFrom":makeQuery(id+"F18.opExtrude","SWEPT_EDGE",EDGE,{"disambiguationData":[OSD([sQuery(id+"F16.wireOp",EDGE,"E54.bottom"),sQuery(id+"F16.wireOp",EDGE,"E54.left")])]})});
            fillet(context, id + "F19", {"entities" : qUnion([Q0, Q1]), "radius" : 0.8 * mm, "tangentPropagation" : true, "allowEdgeOverflow" : false});
        }
    });
